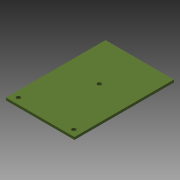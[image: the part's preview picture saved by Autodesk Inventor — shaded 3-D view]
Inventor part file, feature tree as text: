
AUTODESK INVENTOR PART (.ipt)
format: ipt  version: 2015 (Build 190159000, 159)  size: 81,408 bytes
history: native  units: mm
features: extrude x1, sketch x1
ambient origin geometry x8: Origin, YZ Plane, XZ Plane, XY Plane, X Axis, Y Axis, Z Axis, Center Point
bodies: Volumenkörper1 (feature_tree)
feature tree (2):
  extrude  "Extrusion1"  Depth=55.0mm
  sketch  "Skizze1"  dims[d0=80.0mm d1=55.0mm d2=3.2mm d3=3.2mm d4=3.2mm d5=5.0mm d6=5.0mm d7=49.5mm d8=5.0mm d9=47.0mm d10=28.0mm d11=2.0mm d12=0.0mm]
